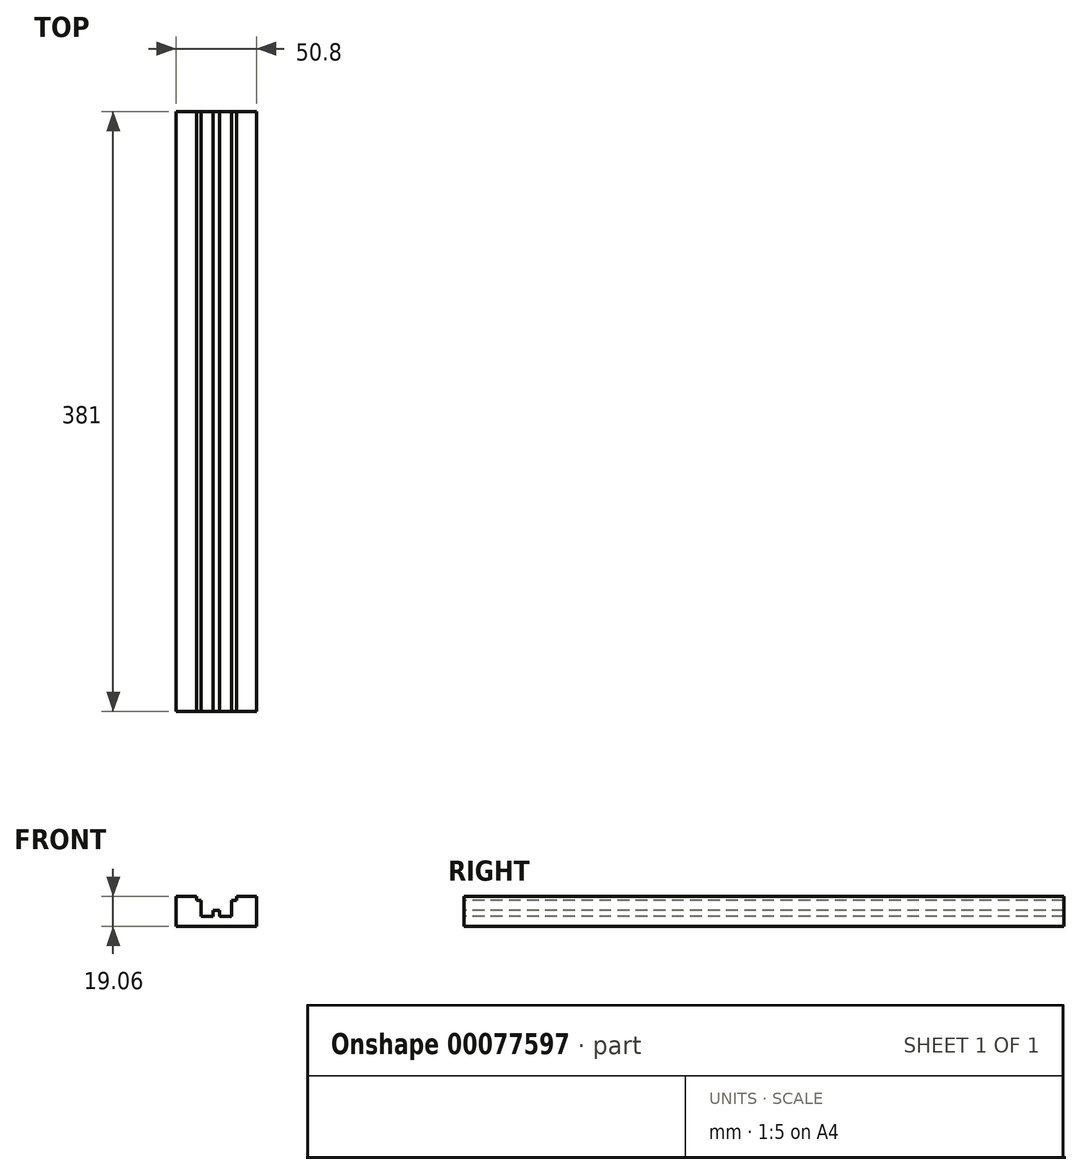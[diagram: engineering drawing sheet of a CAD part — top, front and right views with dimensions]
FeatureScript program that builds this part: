
annotation { "Feature Type Name" : "Feature", "Feature Type Description" : "" }
export const myFeature = defineFeature(function(context is Context, id is Id, definition is map)
    precondition{}
    {
        {
            var Q0;
            Q0=qCreatedBy(makeId("Front.planeOp"),FACE);
            var sketch = newSketch(context, id + "F0", { "sketchPlane" : qUnion([Q0])});
            skLineSegment(sketch, "E0.bottom", {"start": v(25.4, 9.53) * mm, "end": v(12.7, 9.53) * mm});
            skLineSegment(sketch, "E0.top", {"start": v(25.4, -9.52) * mm, "end": v(-25.4, -9.52) * mm});
            skLineSegment(sketch, "E0.left", {"start": v(25.4, 9.53) * mm, "end": v(25.4, -9.52) * mm});
            skLineSegment(sketch, "E0.right", {"start": v(-25.4, 9.53) * mm, "end": v(-25.4, -9.52) * mm});
            skPoint(sketch, "E0.middle", {"position": v(0, 0) * mm});
            skLineSegment(sketch, "E1.top", {"start": v(9.53, -3.17) * mm, "end": v(1.97, -3.17) * mm});
            skLineSegment(sketch, "E1.left", {"start": v(9.53, 6.99) * mm, "end": v(9.53, -3.17) * mm});
            skLineSegment(sketch, "E1.right", {"start": v(-9.53, 6.99) * mm, "end": v(-9.52, -3.17) * mm});
            skPoint(sketch, "E1.middle", {"position": v(0, 3.18) * mm});
            skLineSegment(sketch, "E2.top", {"start": v(12.7, 6.99) * mm, "end": v(9.53, 6.99) * mm});
            skLineSegment(sketch, "E2.left", {"start": v(12.7, 9.53) * mm, "end": v(12.7, 6.99) * mm});
            skLineSegment(sketch, "E2.right", {"start": v(-12.7, 9.53) * mm, "end": v(-12.7, 6.99) * mm});
            skPoint(sketch, "E2.middle", {"position": v(0, 8.26) * mm});
            skLineSegment(sketch, "E3.top", {"start": v(1.97, 0.63) * mm, "end": v(-1.97, 0.63) * mm});
            skLineSegment(sketch, "E3.left", {"start": v(1.97, -3.18) * mm, "end": v(1.97, 0.63) * mm});
            skLineSegment(sketch, "E3.right", {"start": v(-1.97, -3.18) * mm, "end": v(-1.97, 0.63) * mm});
            skPoint(sketch, "E3.middle", {"position": v(0, -1.27) * mm});
            skPoint(sketch, "E3.centerSnap0", {"position": v(0, -3.17) * mm});
            skLineSegment(sketch, "E4.trimOffspring", {"start": v(-9.53, 6.99) * mm, "end": v(-12.7, 6.99) * mm});
            skLineSegment(sketch, "E5.trimOffspring", {"start": v(-1.97, -3.17) * mm, "end": v(-9.52, -3.17) * mm});
            skLineSegment(sketch, "E6.trimOffspring", {"start": v(-12.7, 9.53) * mm, "end": v(-25.4, 9.53) * mm});
            skSolve(sketch);
        }
        {
            var Q0;
            Q0 = qSketchRegion(id + "F0", true);
            extrude(context, id + "F1", {"entities" : qUnion([Q0]), "oppositeDirection" : true, "depth" : 381 * mm});
        }
    });
